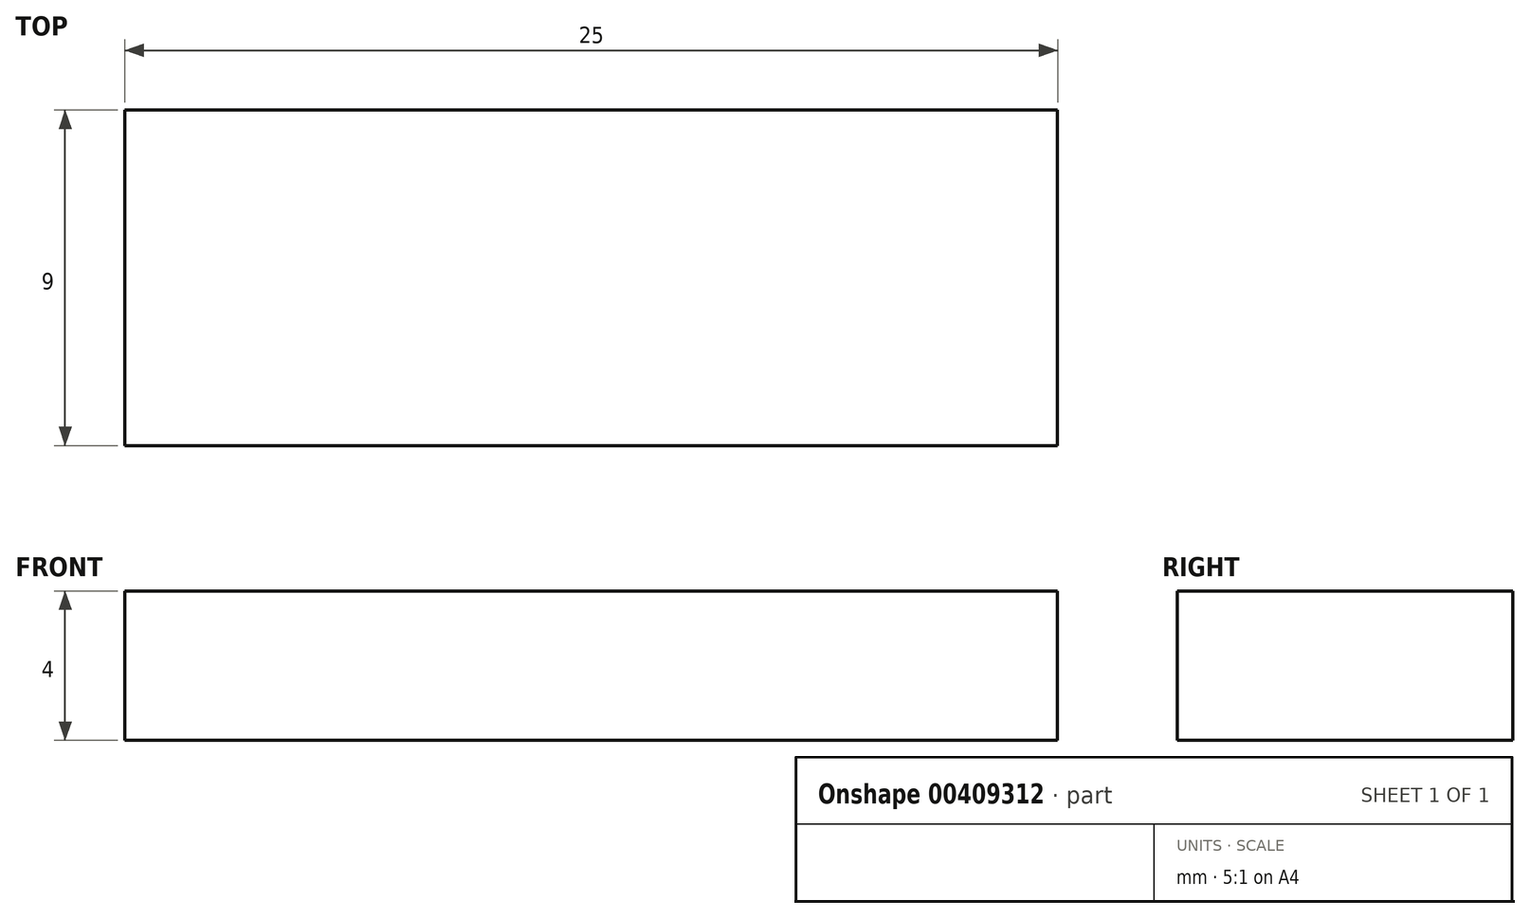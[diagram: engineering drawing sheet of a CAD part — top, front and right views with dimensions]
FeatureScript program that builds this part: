
annotation { "Feature Type Name" : "Feature", "Feature Type Description" : "" }
export const myFeature = defineFeature(function(context is Context, id is Id, definition is map)
    precondition{}
    {
        {
            var Q0;
            Q0=qCreatedBy(makeId("Top.planeOp"),FACE);
            var sketch = newSketch(context, id + "F0", { "sketchPlane" : qUnion([Q0])});
            skLineSegment(sketch, "E0.bottom", {"start": v(-13.85, 0.1) * mm, "end": v(11.15, 0.1) * mm});
            skLineSegment(sketch, "E0.top", {"start": v(-13.85, -8.9) * mm, "end": v(11.15, -8.9) * mm});
            skLineSegment(sketch, "E0.left", {"start": v(-13.85, 0.1) * mm, "end": v(-13.85, -8.9) * mm});
            skLineSegment(sketch, "E0.right", {"start": v(11.15, 0.1) * mm, "end": v(11.15, -8.9) * mm});
            skSolve(sketch);
        }
        {
            var Q0;
            Q0=makeQuery(id+"F0.imprint","IMPRINT",FACE,{"disambiguationData":[TD([[makeQuery(id+"F0.imprint","IMPRINT",EDGE,{"derivedFrom":sQuery(id+"F0.wireOp",EDGE,"E0.bottom")}),-1.0]])]});
            extrude(context, id + "F1", {"entities" : qUnion([Q0]), "depth" : 4 * mm});
        }
        {
            var Q0;
            Q0=makeQuery(id+"F1.opExtrude","CAP_FACE",FACE,{"disambiguationData":[OSD([sQuery(id+"F0.wireOp",EDGE,"E0.bottom"),sQuery(id+"F0.wireOp",EDGE,"E0.top"),sQuery(id+"F0.wireOp",EDGE,"E0.left"),sQuery(id+"F0.wireOp",EDGE,"E0.right")])],"isStart":false});
            var sketch = newSketch(context, id + "F2", { "sketchPlane" : qUnion([Q0])});
            skCircle(sketch, "E1", {"center": v(-11.5, -4.57) * mm, "radius": 0.9 * mm});
            skSolve(sketch);
        }
        {
            var Q0;
            Q0=sQuery(id+"F2.wireOp",EDGE,"E1");
            extrude(context, id + "F3", {"bodyType" : ToolBodyType.SURFACE, "operationType" : NewBodyOperationType.ADD, "surfaceEntities" : qUnion([Q0]), "oppositeDirection" : true, "depth" : 10 * mm});
        }
    });
